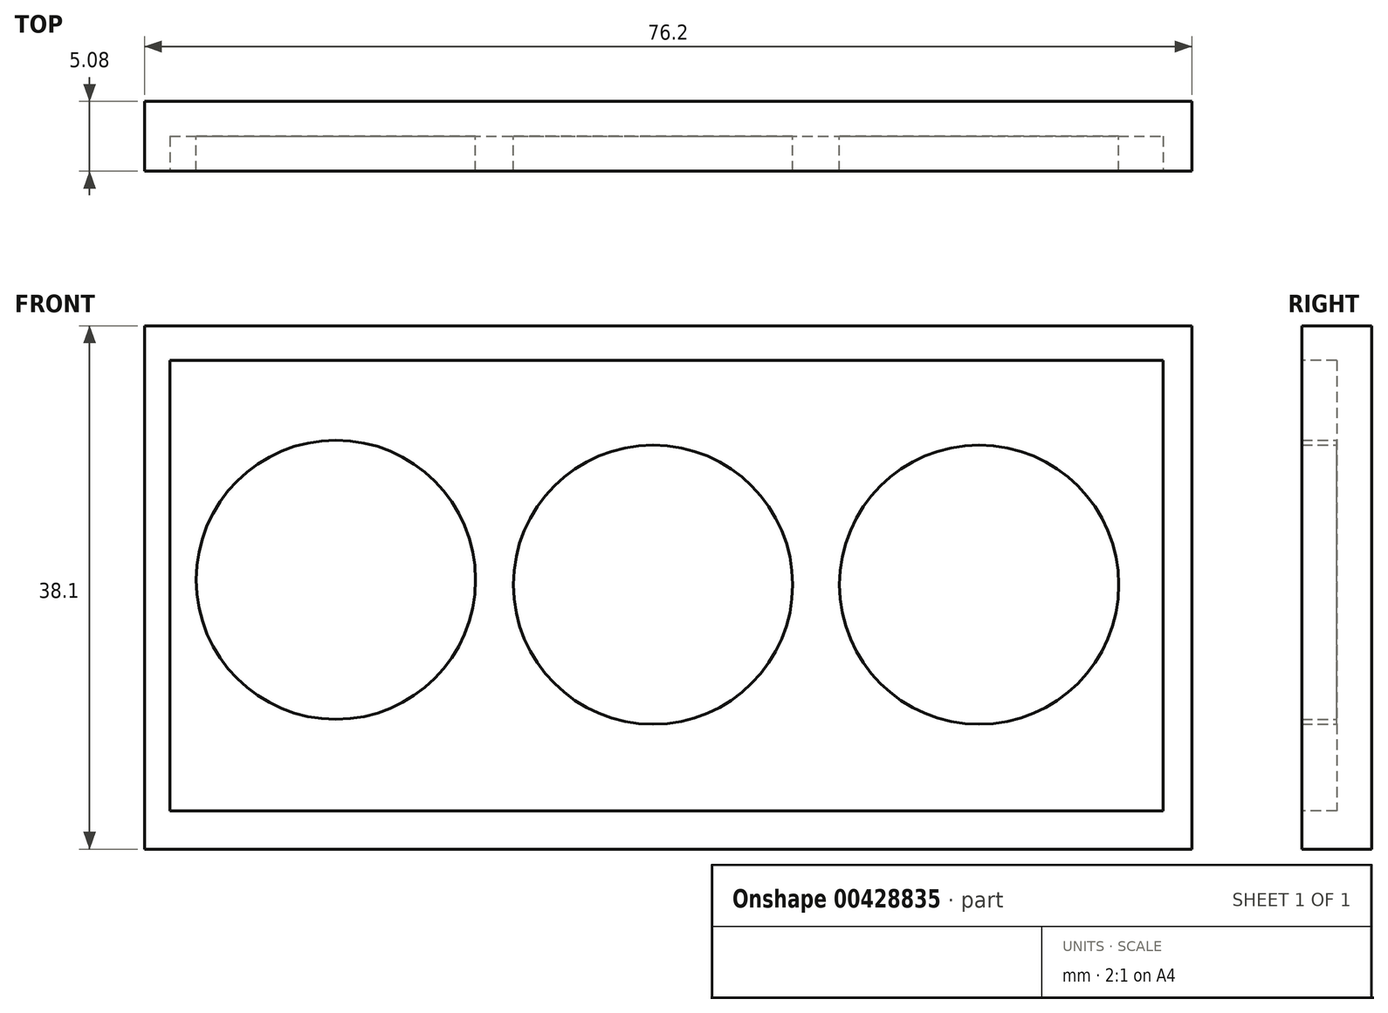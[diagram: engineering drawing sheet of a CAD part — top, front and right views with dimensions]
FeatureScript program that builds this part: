
annotation { "Feature Type Name" : "Feature", "Feature Type Description" : "" }
export const myFeature = defineFeature(function(context is Context, id is Id, definition is map)
    precondition{}
    {
        {
            var Q0;
            Q0=qCreatedBy(makeId("Front.planeOp"),FACE);
            var sketch = newSketch(context, id + "F0", { "sketchPlane" : qUnion([Q0])});
            skLineSegment(sketch, "E0.bottom", {"start": v(0, 0) * mm, "end": v(76.2, 0) * mm});
            skLineSegment(sketch, "E0.top", {"start": v(0, -38.1) * mm, "end": v(76.2, -38.1) * mm});
            skLineSegment(sketch, "E0.left", {"start": v(0, 0) * mm, "end": v(0, -38.1) * mm});
            skLineSegment(sketch, "E0.right", {"start": v(76.2, 0) * mm, "end": v(76.2, -38.1) * mm});
            skSolve(sketch);
        }
        {
            var Q0;
            Q0 = qSketchRegion(id + "F0", true);
            extrude(context, id + "F1", {"entities" : qUnion([Q0]), "depth" : 5.08 * mm});
        }
        {
            var Q0;
            Q0=makeQuery(id+"F1.opExtrude","CAP_FACE",FACE,{"disambiguationData":[OSD([sQuery(id+"F0.wireOp",EDGE,"E0.bottom"),sQuery(id+"F0.wireOp",EDGE,"E0.top"),sQuery(id+"F0.wireOp",EDGE,"E0.left"),sQuery(id+"F0.wireOp",EDGE,"E0.right")])],"isStart":false});
            var sketch = newSketch(context, id + "F2", { "sketchPlane" : qUnion([Q0])});
            skLineSegment(sketch, "E1.bottom", {"start": v(1.85, -2.52) * mm, "end": v(74.12, -2.52) * mm});
            skLineSegment(sketch, "E1.top", {"start": v(1.85, -35.32) * mm, "end": v(74.12, -35.32) * mm});
            skLineSegment(sketch, "E1.left", {"start": v(1.85, -2.52) * mm, "end": v(1.85, -35.32) * mm});
            skLineSegment(sketch, "E1.right", {"start": v(74.12, -2.52) * mm, "end": v(74.12, -35.32) * mm});
            skSolve(sketch);
        }
        {
            var Q0;
            Q0 = qSketchRegion(id + "F2", true);
            extrude(context, id + "F3", {"entities" : qUnion([Q0]), "operationType" : NewBodyOperationType.REMOVE, "oppositeDirection" : true, "depth" : 2.54 * mm});
        }
        {
            var Q0;
            Q0=makeQuery(id+"F3.boolean.opBoolean","COPY",FACE,{"derivedFrom":makeQuery(id+"F3.opExtrude","CAP_FACE",FACE,{"disambiguationData":[OSD([sQuery(id+"F2.wireOp",EDGE,"E1.bottom"),sQuery(id+"F2.wireOp",EDGE,"E1.top"),sQuery(id+"F2.wireOp",EDGE,"E1.left"),sQuery(id+"F2.wireOp",EDGE,"E1.right")])],"isStart":false})});
            var sketch = newSketch(context, id + "F4", { "sketchPlane" : qUnion([Q0])});
            skCircle(sketch, "E2", {"center": v(13.92, -18.49) * mm, "radius": 10.16 * mm});
            skCircle(sketch, "E3", {"center": v(37, -18.84) * mm, "radius": 10.16 * mm});
            skCircle(sketch, "E4", {"center": v(60.72, -18.85) * mm, "radius": 10.16 * mm});
            skSolve(sketch);
        }
        {
            var Q0;
            Q0 = qSketchRegion(id + "F4", true);
            extrude(context, id + "F5", {"entities" : qUnion([Q0]), "operationType" : NewBodyOperationType.ADD, "depth" : 2.54 * mm});
        }
    });
